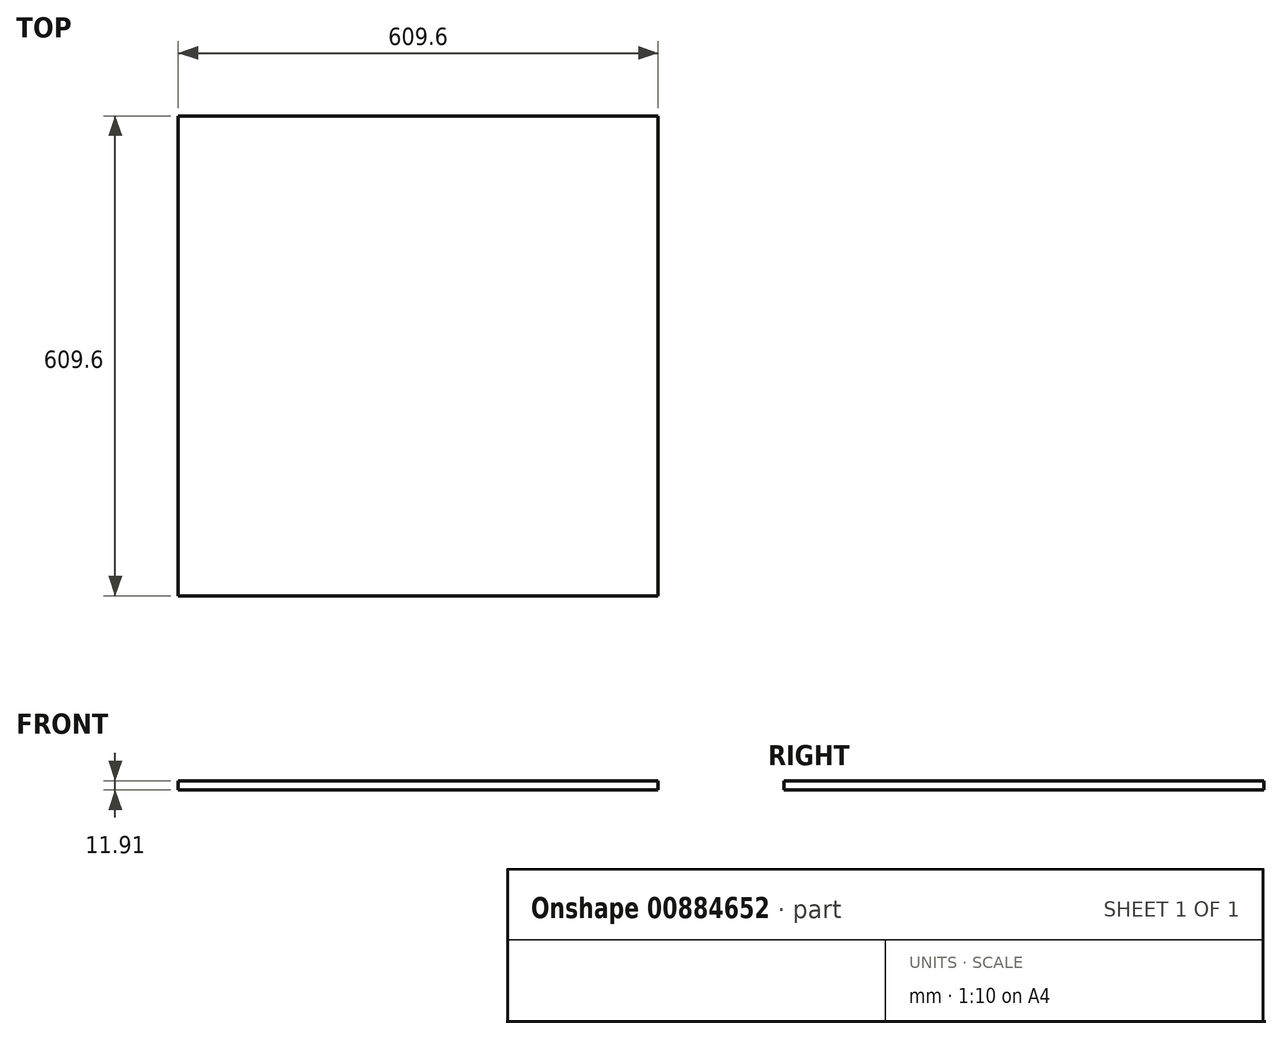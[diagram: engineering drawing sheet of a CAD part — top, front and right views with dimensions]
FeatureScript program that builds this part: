
annotation { "Feature Type Name" : "Feature", "Feature Type Description" : "" }
export const myFeature = defineFeature(function(context is Context, id is Id, definition is map)
    precondition{}
    {
        {
            var Q0;
            Q0=qCreatedBy(makeId("Top.planeOp"),FACE);
            var sketch = newSketch(context, id + "F0", { "sketchPlane" : qUnion([Q0])});
            skLineSegment(sketch, "E0.bottom", {"start": v(-304.8, 309.7) * mm, "end": v(304.8, 309.7) * mm});
            skLineSegment(sketch, "E0.top", {"start": v(-304.8, -299.9) * mm, "end": v(304.8, -299.9) * mm});
            skLineSegment(sketch, "E0.left", {"start": v(-304.8, 309.7) * mm, "end": v(-304.8, -299.9) * mm});
            skLineSegment(sketch, "E0.right", {"start": v(304.8, 309.7) * mm, "end": v(304.8, -299.9) * mm});
            skSolve(sketch);
        }
        {
            var Q0;
            Q0 = qSketchRegion(id + "F0", true);
            extrude(context, id + "F1", {"entities" : qUnion([Q0]), "depth" : 11.9 * mm, "offsetDistance" : 25.4 * mm});
        }
    });
